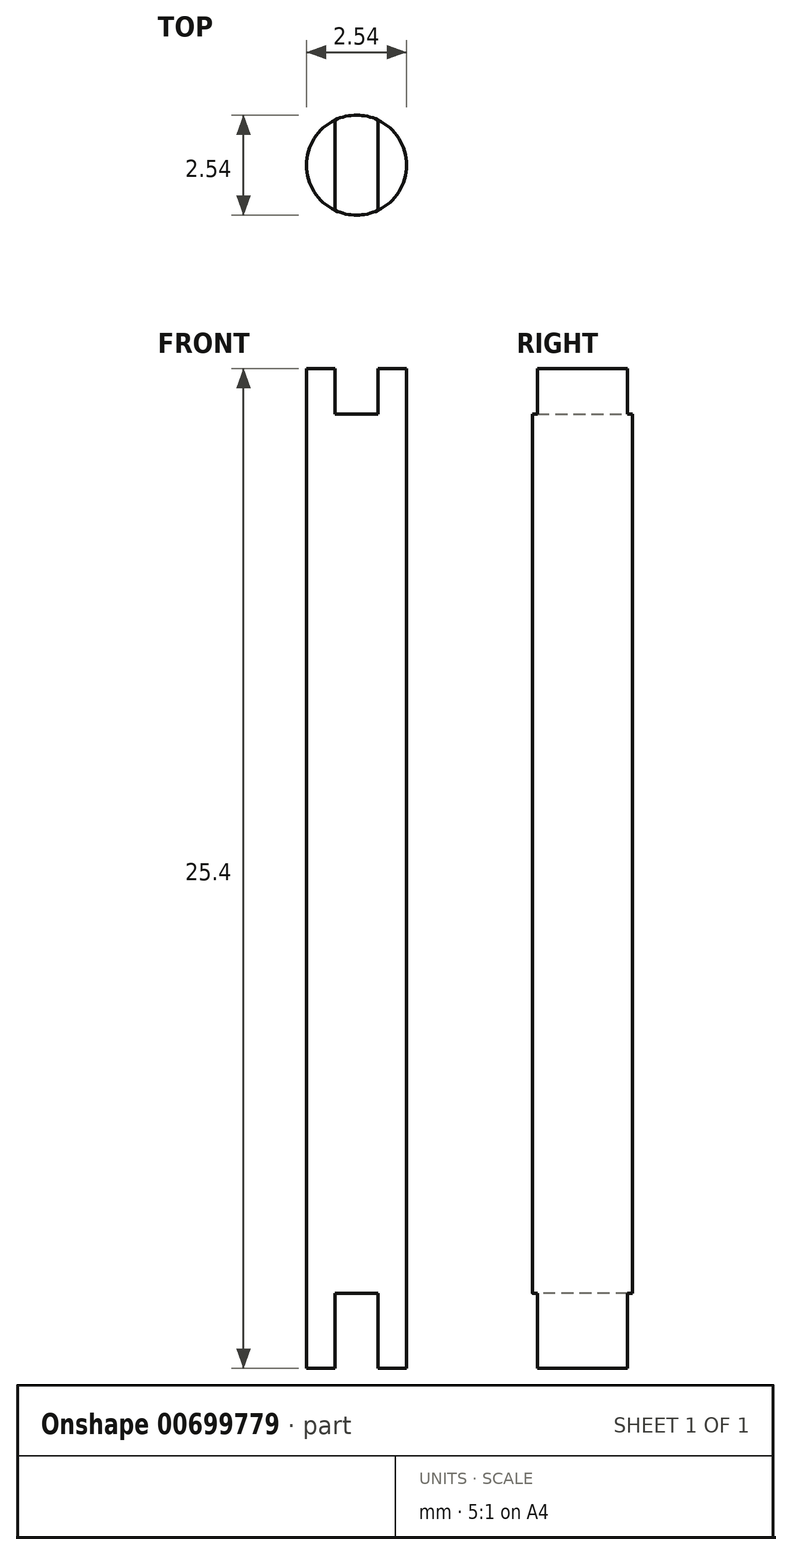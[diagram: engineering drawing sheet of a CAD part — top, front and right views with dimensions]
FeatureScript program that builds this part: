
annotation { "Feature Type Name" : "Feature", "Feature Type Description" : "" }
export const myFeature = defineFeature(function(context is Context, id is Id, definition is map)
    precondition{}
    {
        {
            var Q0;
            Q0=qCreatedBy(makeId("Top.planeOp"),FACE);
            var sketch = newSketch(context, id + "F0", { "sketchPlane" : qUnion([Q0])});
            skCircle(sketch, "E0", {"center": v(0, 0) * mm, "radius": 1.27 * mm});
            skSolve(sketch);
        }
        {
            var Q0;
            Q0=makeQuery(id+"F0.imprint","IMPRINT",FACE,{"disambiguationData":[TD([[makeQuery(id+"F0.imprint","IMPRINT",EDGE,{"derivedFrom":sQuery(id+"F0.wireOp",EDGE,"E0")}),1.0]])]});
            extrude(context, id + "F1", {"entities" : qUnion([Q0]), "depth" : 25.4 * mm, "offsetDistance" : 25.4 * mm});
        }
        {
            var Q0;
            Q0=qCreatedBy(makeId("Front.planeOp"),FACE);
            var sketch = newSketch(context, id + "F2", { "sketchPlane" : qUnion([Q0])});
            skLineSegment(sketch, "E1.bottom", {"start": v(0.55, 24.24) * mm, "end": v(-0.55, 24.24) * mm});
            skLineSegment(sketch, "E1.top", {"start": v(0.55, 28.05) * mm, "end": v(-0.55, 28.05) * mm});
            skLineSegment(sketch, "E1.left", {"start": v(0.55, 24.24) * mm, "end": v(0.55, 28.05) * mm});
            skLineSegment(sketch, "E1.right", {"start": v(-0.55, 24.24) * mm, "end": v(-0.55, 28.05) * mm});
            skPoint(sketch, "E1.middle", {"position": v(0, 26.15) * mm});
            skSolve(sketch);
        }
        {
            var Q0;
            Q0=makeQuery(id+"F2.imprint","IMPRINT",FACE,{"disambiguationData":[TD([[makeQuery(id+"F2.imprint","IMPRINT",EDGE,{"derivedFrom":sQuery(id+"F2.wireOp",EDGE,"E1.bottom")}),-1.0]])]});
            extrude(context, id + "F3", {"entities" : qUnion([Q0]), "operationType" : NewBodyOperationType.REMOVE, "depth" : 9.4 * mm, "offsetDistance" : 25.4 * mm});
        }
        {
            var Q0;
            Q0 = qSketchRegion(id + "F2", true);
            extrude(context, id + "F4", {"entities" : qUnion([Q0]), "operationType" : NewBodyOperationType.REMOVE, "oppositeDirection" : true, "depth" : 25.4 * mm, "offsetDistance" : 25.4 * mm});
        }
        {
            var Q0;
            Q0=qCreatedBy(makeId("Front.planeOp"),FACE);
            var sketch = newSketch(context, id + "F5", { "sketchPlane" : qUnion([Q0])});
            skLineSegment(sketch, "E2.bottom", {"start": v(0.55, 1.9) * mm, "end": v(-0.55, 1.9) * mm});
            skLineSegment(sketch, "E2.top", {"start": v(0.55, -1.9) * mm, "end": v(-0.55, -1.9) * mm});
            skLineSegment(sketch, "E2.left", {"start": v(0.55, 1.9) * mm, "end": v(0.55, -1.9) * mm});
            skLineSegment(sketch, "E2.right", {"start": v(-0.55, 1.9) * mm, "end": v(-0.55, -1.9) * mm});
            skPoint(sketch, "E2.middle", {"position": v(0, 0) * mm});
            skSolve(sketch);
        }
        {
            var Q0;
            Q0=makeQuery(id+"F5.imprint","IMPRINT",FACE,{"disambiguationData":[TD([[makeQuery(id+"F5.imprint","IMPRINT",EDGE,{"derivedFrom":sQuery(id+"F5.wireOp",EDGE,"E2.bottom")}),1.0]])]});
            extrude(context, id + "F6", {"entities" : qUnion([Q0]), "operationType" : NewBodyOperationType.REMOVE, "oppositeDirection" : true, "depth" : 25.4 * mm, "offsetDistance" : 25.4 * mm});
        }
        {
            var Q0;
            Q0=makeQuery(id+"F5.imprint","IMPRINT",FACE,{"disambiguationData":[TD([[makeQuery(id+"F5.imprint","IMPRINT",EDGE,{"derivedFrom":sQuery(id+"F5.wireOp",EDGE,"E2.bottom")}),1.0]])]});
            extrude(context, id + "F7", {"entities" : qUnion([Q0]), "operationType" : NewBodyOperationType.REMOVE, "depth" : 25.4 * mm, "offsetDistance" : 25.4 * mm});
        }
        {
            var Q0;
            Q0 = qSketchRegion(id + "F2", true);
            extrude(context, id + "F8", {"entities" : qUnion([Q0]), "operationType" : NewBodyOperationType.REMOVE, "oppositeDirection" : true, "depth" : 25.4 * mm, "offsetDistance" : 25.4 * mm});
        }
    });
